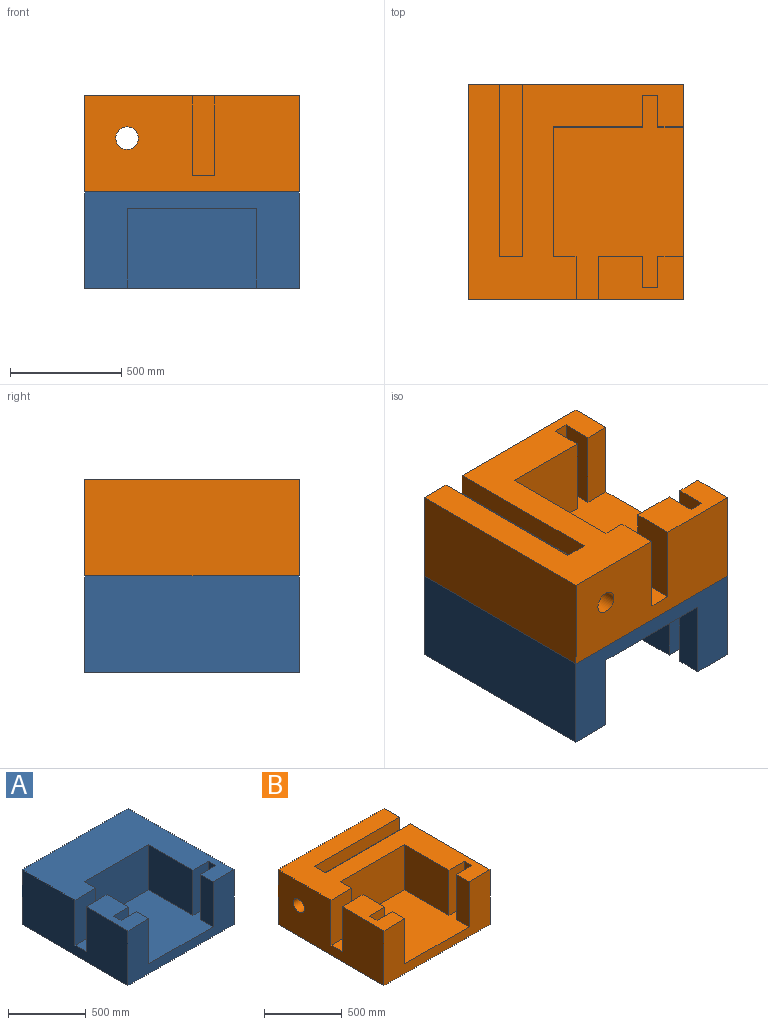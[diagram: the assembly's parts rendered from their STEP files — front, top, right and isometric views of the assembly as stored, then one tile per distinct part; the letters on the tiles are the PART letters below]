
ASSEMBLY  parts=2 mates=1
PART A: 22 faces, bbox 965.2x965.2x431.8 mm
  f0: plane 914.4x584.2mm, normal (0,0,1), area 379805.7mm2, adj f1,f2,f6,f7,f8,f9,f10,f11
  f1: plane 965.2x431.8mm, normal (-1,0,0), area 380644.4mm2, adj f0,f2,f4,f5,f7,f12,f20,f21
  f2: plane 965.2x431.8mm, normal (0,-1,0), area 209031.8mm2, adj f0,f1,f3,f5,f8,f12,f19,f21
  f3: plane 965.2x431.8mm, normal (1,0,0), area 416773.4mm2, adj f2,f4,f5,f21
  f4: plane 965.2x431.8mm, normal (0,1,0), area 416773.4mm2, adj f1,f3,f5,f21
  f5: plane 965.2x965.2mm, normal (0,0,-1), area 931611mm2, adj f1,f2,f3,f4
  f6: plane 355.6x198.12mm, normal (1,0,0), area 70451.5mm2, adj f0,f7,f11,f12
  f7: plane 355.6x190.5mm, normal (0,1,0), area 67741.8mm2, adj f0,f1,f6,f12
  f8: plane 355.6x114.3mm, normal (1,0,0), area 40645.1mm2, adj f0,f2,f9,f12
  f9: plane 355.6x139.7mm, normal (0,1,0), area 49677.3mm2, adj f0,f8,f10,f12
  f10: plane 355.6x68.58mm, normal (1,0,0), area 24387mm2, adj f0,f9,f11,f12
  f11: plane 355.6x139.7mm, normal (0,-1,0), area 49677.3mm2, adj f0,f6,f10,f12
  f12: plane 381x190.5mm, normal (0,0,1), area 62999.9mm2, adj f1,f2,f6,f7,f8,f9,f10,f11
  f13: plane 355.6x101.6mm, normal (1,0,0), area 36129mm2, adj f0,f14,f20,f21
  f14: plane 584.2x355.6mm, normal (0,-1,0), area 207741.5mm2, adj f0,f13,f15,f21
  f15: plane 401.32x355.6mm, normal (-1,0,0), area 142709.4mm2, adj f0,f14,f16,f21
  f16: plane 355.6x139.7mm, normal (0,-1,0), area 49677.3mm2, adj f0,f15,f17,f21
  f17: plane 355.6x68.58mm, normal (-1,0,0), area 24387mm2, adj f0,f16,f18,f21
  f18: plane 355.6x139.7mm, normal (0,1,0), area 49677.3mm2, adj f0,f17,f19,f21
  f19: plane 355.6x114.3mm, normal (-1,0,0), area 40645.1mm2, adj f0,f2,f18,f21
  f20: plane 355.6x190.5mm, normal (0,-1,0), area 67741.8mm2, adj f0,f1,f13,f21
  f21: plane 965.2x965.2mm, normal (0,0,1), area 488805.5mm2, adj f1,f2,f3,f4,f13,f14,f15,f16
PART B: 33 faces, bbox 965.2x965.2x431.8 mm
  f0: plane 965.2x431.8mm, normal (1,0,0), area 378257mm2, adj f1,f4,f5,f6,f22,f23,f24,f25
  f1: plane 965.2x965.2mm, normal (0,0,1), area 408147.9mm2, adj f0,f3,f4,f5,f14,f15,f16,f17
  f2: plane 914.4x584.2mm, normal (0,0,1), area 379805.7mm2, adj f3,f4,f7,f8,f9,f10,f11,f12
  f3: plane 965.2x431.8mm, normal (-1,0,0), area 372537.1mm2, adj f1,f2,f4,f5,f6,f8,f13,f21
  f4: plane 965.2x431.8mm, normal (0,-1,0), area 209031.8mm2, adj f0,f1,f2,f3,f6,f9,f13,f20
  f5: plane 965.2x431.8mm, normal (0,1,0), area 416773.4mm2, adj f0,f1,f3,f6
  f6: plane 965.2x965.2mm, normal (0,0,-1), area 931611mm2, adj f0,f3,f4,f5
  f7: plane 355.6x198.12mm, normal (1,0,0), area 70451.5mm2, adj f2,f8,f12,f13
  f8: plane 355.6x190.5mm, normal (0,1,0), area 67741.8mm2, adj f2,f3,f7,f13
  f9: plane 355.6x114.3mm, normal (1,0,0), area 40645.1mm2, adj f2,f4,f10,f13
  f10: plane 355.6x139.7mm, normal (0,1,0), area 49677.3mm2, adj f2,f9,f11,f13
  f11: plane 355.6x68.58mm, normal (1,0,0), area 24387mm2, adj f2,f10,f12,f13
  f12: plane 355.6x139.7mm, normal (0,-1,0), area 49677.3mm2, adj f2,f7,f11,f13
  f13: plane 381x190.5mm, normal (0,0,1), area 62999.9mm2, adj f3,f4,f7,f8,f9,f10,f11,f12
  f14: plane 355.6x101.6mm, normal (1,0,0), area 36129mm2, adj f1,f2,f15,f21
  f15: plane 584.2x355.6mm, normal (0,-1,0), area 207741.5mm2, adj f1,f2,f14,f16
  f16: plane 401.32x355.6mm, normal (-1,0,0), area 142709.4mm2, adj f1,f2,f15,f17
  f17: plane 355.6x139.7mm, normal (0,-1,0), area 49677.3mm2, adj f1,f2,f16,f18
  f18: plane 355.6x68.58mm, normal (-1,0,0), area 24387mm2, adj f1,f2,f17,f19
  f19: plane 355.6x139.7mm, normal (0,1,0), area 49677.3mm2, adj f1,f2,f18,f20
  f20: plane 355.6x114.3mm, normal (-1,0,0), area 40645.1mm2, adj f1,f2,f4,f19
  f21: plane 355.6x190.5mm, normal (0,-1,0), area 67741.8mm2, adj f1,f2,f3,f14
  f22: plane 774.7x99.42mm, normal (0,1,0), area 77020.3mm2, adj f0,f1,f23,f31
  f23: plane 774.7x0mm, normal (0,0,-1), area 1.8mm2, adj f0,f22,f24,f31
  f24: plane 774.7x90.17mm, normal (0,0.87,-0.5), area 80661.3mm2, adj f0,f23,f25,f31
  f25: plane 774.7x90.17mm, normal (0,0.87,0.5), area 80661.3mm2, adj f0,f24,f26,f31
  f26: plane 774.7x104.12mm, normal (0,0,1), area 80661.3mm2, adj f0,f25,f27,f31
  f27: plane 774.7x90.17mm, normal (0,-0.87,0.5), area 80661.3mm2, adj f0,f26,f28,f31
  f28: plane 774.7x90.17mm, normal (0,-0.87,-0.5), area 80661.3mm2, adj f0,f27,f29,f31
  f29: plane 774.7x0mm, normal (0,0,-1), area 1.8mm2, adj f0,f28,f30,f31
  f30: plane 774.7x99.42mm, normal (0,-1,0), area 77020.3mm2, adj f0,f1,f29,f31
  f31: plane 279.76x208.24mm, normal (1,0,0), area 30409mm2, adj f1,f22,f23,f24,f25,f26,f27,f28
  f32: cylinder r=50.8mm len=190.5mm, axis (1,0,0), area 60804.9mm2, adj f3,f31
PLACE A rot(axis=(0,-1,0),180deg) t=(-328.43,-1531.25,582.12)mm
PLACE B rot(axis=(0,0,1),90deg) t=(-328.43,-1531.25,734.52)mm
MATE fastened A.f5 <-> B.f6  axis (0,0,1) through (-328.43,-1531.25,658.32)mm
